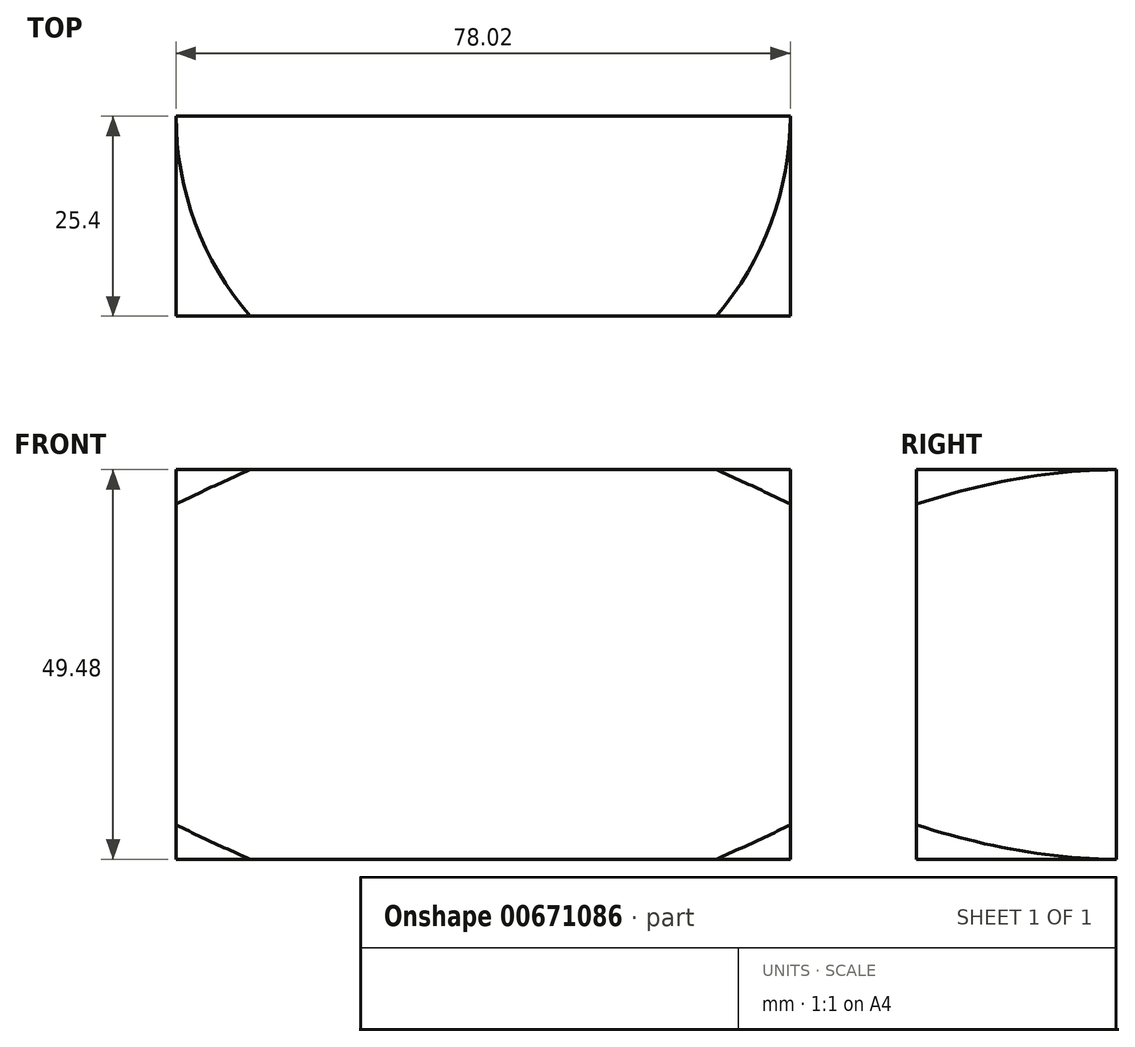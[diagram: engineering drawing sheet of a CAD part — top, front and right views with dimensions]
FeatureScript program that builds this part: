
annotation { "Feature Type Name" : "Feature", "Feature Type Description" : "" }
export const myFeature = defineFeature(function(context is Context, id is Id, definition is map)
    precondition{}
    {
        {
            var Q0;
            Q0=qCreatedBy(makeId("Front.planeOp"),FACE);
            var sketch = newSketch(context, id + "F0", { "sketchPlane" : qUnion([Q0])});
            skLineSegment(sketch, "E0.bottom", {"start": v(-39, 24.74) * mm, "end": v(39, 24.74) * mm});
            skLineSegment(sketch, "E0.top", {"start": v(-39, -24.74) * mm, "end": v(39, -24.74) * mm});
            skLineSegment(sketch, "E0.left", {"start": v(-39, 24.74) * mm, "end": v(-39, -24.74) * mm});
            skLineSegment(sketch, "E0.right", {"start": v(39, 24.74) * mm, "end": v(39, -24.74) * mm});
            skPoint(sketch, "E0.middle", {"position": v(0, 0) * mm});
            skSolve(sketch);
        }
        {
            var Q0;
            Q0=makeQuery(id+"F0.imprint","IMPRINT",FACE,{"disambiguationData":[TD([[makeQuery(id+"F0.imprint","IMPRINT",EDGE,{"derivedFrom":sQuery(id+"F0.wireOp",EDGE,"E0.bottom")}),-1.0]])]});
            extrude(context, id + "F1", {"entities" : qUnion([Q0]), "depth" : 25.4 * mm, "offsetDistance" : 25.4 * mm});
        }
        {
            var Q0;
            Q0=qCreatedBy(makeId("Front.planeOp"),FACE);
            var sketch = newSketch(context, id + "F2", { "sketchPlane" : qUnion([Q0])});
            skLineSegment(sketch, "E1", {"start": v(0, 25.18) * mm, "end": v(0, -25.18) * mm, "construction": true});
            skLineSegment(sketch, "E2", {"start": v(0, 0) * mm, "end": v(39, 0) * mm, "construction": true});
            skLineSegment(sketch, "E3", {"start": v(39, 24.74) * mm, "end": v(57.69, 24.74) * mm});
            skLineSegment(sketch, "E4", {"start": v(57.69, 24.74) * mm, "end": v(57.69, 13.96) * mm});
            skLineSegment(sketch, "E5", {"start": v(57.69, 13.96) * mm, "end": v(39, 24.74) * mm});
            skLineSegment(sketch, "E6.MirrorCS", {"start": v(39, -24.74) * mm, "end": v(57.69, -24.74) * mm});
            skLineSegment(sketch, "E7.MirrorCS", {"start": v(57.69, -13.96) * mm, "end": v(39, -24.74) * mm});
            skLineSegment(sketch, "E8.MirrorCS", {"start": v(57.69, -24.74) * mm, "end": v(57.69, -13.96) * mm});
            skSolve(sketch);
        }
        {
            var Q0;
            Q0 = qSketchRegion(id + "F2", true);
            var Q1;
            Q1=sQuery(id+"F2.wireOp",EDGE,"E1");
            revolve(context, id + "F3", {"operationType" : NewBodyOperationType.REMOVE, "entities" : qUnion([Q0]), "axis" : qUnion([Q1]), "revolveType" : RevolveType.FULL, "oppositeDirection" : true});
        }
    });
